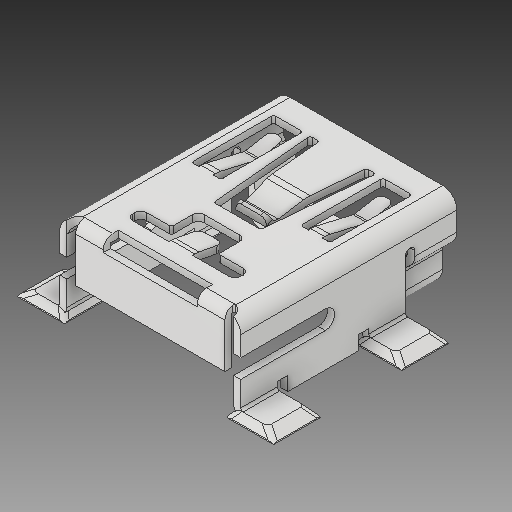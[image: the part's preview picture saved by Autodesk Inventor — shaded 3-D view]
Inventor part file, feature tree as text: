
AUTODESK INVENTOR PART (.ipt)
format: ipt  version: 2019 (Build 230136000, 136)  size: 392,192 bytes
history: native  units: in
note: dims shown in document units (in); Inventor stores cm internally (conversion verified against a paired STEP export)
features: fillet x1
ambient origin geometry x8: Origin, YZ Plane, XZ Plane, XY Plane, X Axis, Y Axis, Z Axis, Center Point
bodies: Solid1 (feature_tree)
feature tree (1):
  fillet  "Fillet14"  [1 undecoded]
note: 1 required parameter value undecoded (feature->parameter linkage not recoverable at this tier; creation-order binding heuristic only, values carry confidence <= 0.55)
